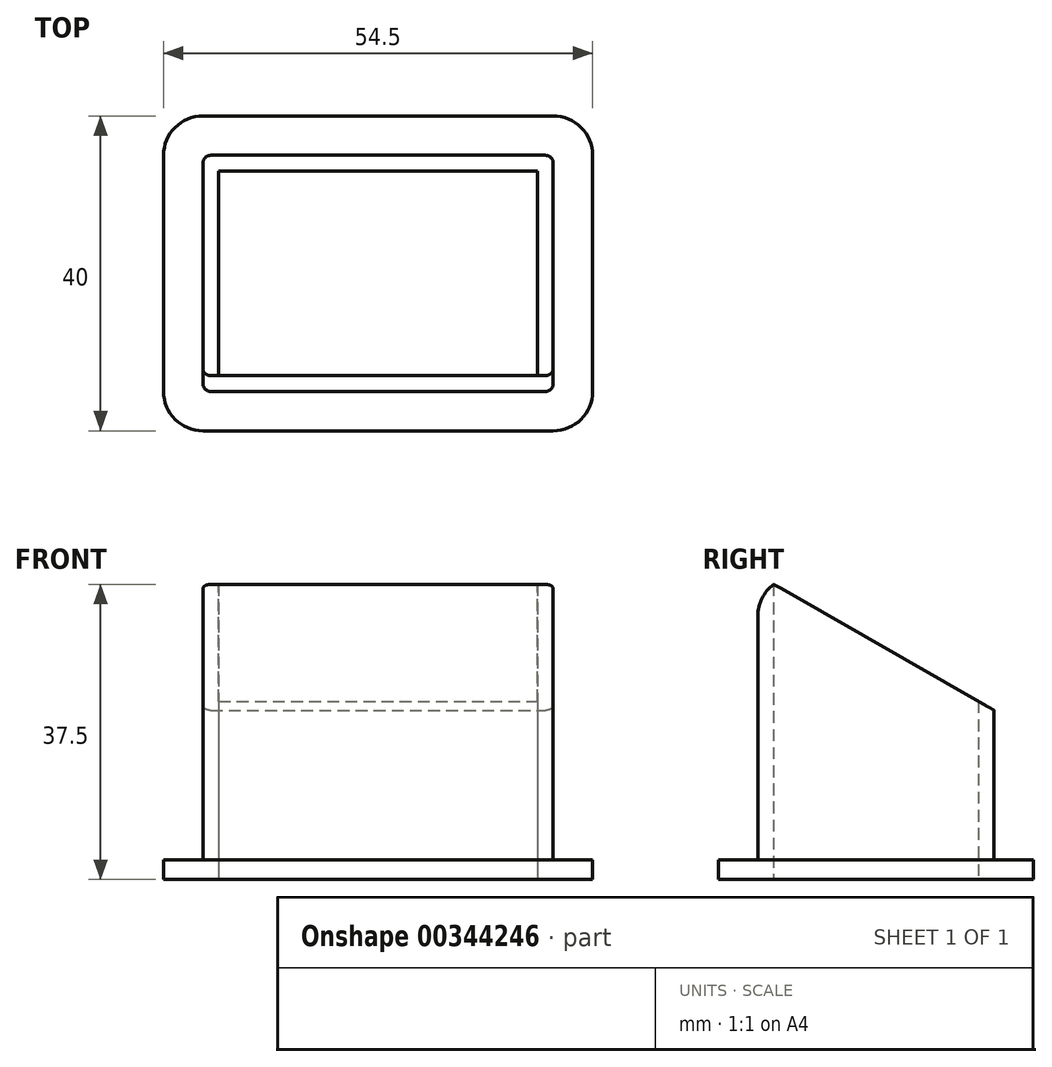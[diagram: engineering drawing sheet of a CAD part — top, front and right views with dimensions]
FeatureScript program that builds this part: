
annotation { "Feature Type Name" : "Feature", "Feature Type Description" : "" }
export const myFeature = defineFeature(function(context is Context, id is Id, definition is map)
    precondition{}
    {
        {
            var Q0;
            Q0=qCreatedBy(makeId("Top.planeOp"),FACE);
            var sketch = newSketch(context, id + "F0", { "sketchPlane" : qUnion([Q0])});
            skLineSegment(sketch, "E0.bottom", {"start": v(-27.25, 20) * mm, "end": v(27.25, 20) * mm});
            skLineSegment(sketch, "E0.top", {"start": v(-27.25, -20) * mm, "end": v(27.25, -20) * mm});
            skLineSegment(sketch, "E0.left", {"start": v(-27.25, 20) * mm, "end": v(-27.25, -20) * mm});
            skLineSegment(sketch, "E0.right", {"start": v(27.25, 20) * mm, "end": v(27.25, -20) * mm});
            skPoint(sketch, "E0.middle", {"position": v(0, 0) * mm});
            skSolve(sketch);
        }
        {
            var Q0;
            Q0=makeQuery(id+"F0.imprint","IMPRINT",FACE,{"disambiguationData":[TD([[makeQuery(id+"F0.imprint","IMPRINT",EDGE,{"derivedFrom":sQuery(id+"F0.wireOp",EDGE,"E0.bottom")}),-1.0]])]});
            extrude(context, id + "F1", {"entities" : qUnion([Q0]), "depth" : 2.5 * mm});
        }
        {
            var Q0;
            Q0=makeQuery(id+"F1.opExtrude","CAP_FACE",FACE,{"disambiguationData":[OSD([sQuery(id+"F0.wireOp",EDGE,"E0.bottom"),sQuery(id+"F0.wireOp",EDGE,"E0.top"),sQuery(id+"F0.wireOp",EDGE,"E0.left"),sQuery(id+"F0.wireOp",EDGE,"E0.right")])],"isStart":false});
            var sketch = newSketch(context, id + "F2", { "sketchPlane" : qUnion([Q0])});
            skLineSegment(sketch, "E1.bottom", {"start": v(-22.25, 15) * mm, "end": v(22.25, 15) * mm});
            skLineSegment(sketch, "E1.top", {"start": v(-22.25, -15) * mm, "end": v(22.25, -15) * mm});
            skLineSegment(sketch, "E1.left", {"start": v(-22.25, 15) * mm, "end": v(-22.25, -15) * mm});
            skLineSegment(sketch, "E1.right", {"start": v(22.25, 15) * mm, "end": v(22.25, -15) * mm});
            skPoint(sketch, "E1.middle", {"position": v(0, 0) * mm});
            skSolve(sketch);
        }
        {
            var Q0;
            Q0 = qSketchRegion(id + "F2", true);
            extrude(context, id + "F3", {"entities" : qUnion([Q0]), "operationType" : NewBodyOperationType.ADD, "depth" : 35 * mm});
        }
        {
            var Q0;
            Q0=makeQuery(id+"F3.opExtrude","CAP_FACE",FACE,{"disambiguationData":[OSD([sQuery(id+"F2.wireOp",EDGE,"E1.bottom"),sQuery(id+"F2.wireOp",EDGE,"E1.top"),sQuery(id+"F2.wireOp",EDGE,"E1.left"),sQuery(id+"F2.wireOp",EDGE,"E1.right")])],"isStart":false});
            shell(context, id + "F4", {"entities" : qUnion([Q0]), "thickness" : 2 * mm});
        }
        {
            var Q0;
            Q0=makeQuery(id+"F4.opShell","OFFSET_FACE",FACE,{"disambiguationData":[OSD([sQuery(id+"F0.wireOp",EDGE,"E0.bottom"),sQuery(id+"F0.wireOp",EDGE,"E0.top"),sQuery(id+"F0.wireOp",EDGE,"E0.left"),sQuery(id+"F0.wireOp",EDGE,"E0.right")])]});
            extrude(context, id + "F5", {"entities" : qUnion([Q0]), "operationType" : NewBodyOperationType.REMOVE, "oppositeDirection" : true, "depth" : 2 * mm});
        }
        {
            var Q0;
            Q0=makeQuery(id+"F3.opExtrude","SWEPT_FACE",FACE,{"disambiguationData":[OSD([sQuery(id+"F2.wireOp",EDGE,"E1.right")])]});
            var sketch = newSketch(context, id + "F6", { "sketchPlane" : qUnion([Q0])});
            skLineSegment(sketch, "E2", {"start": v(15, 2.5) * mm, "end": v(15, 21.5) * mm, "construction": true});
            skLineSegment(sketch, "E3", {"start": v(-15, 37.5) * mm, "end": v(-13, 37.5) * mm, "construction": true});
            skLineSegment(sketch, "E4", {"start": v(15, 21.5) * mm, "end": v(-13, 37.5) * mm});
            skLineSegment(sketch, "E5", {"start": v(-13, 37.5) * mm, "end": v(15, 37.5) * mm});
            skLineSegment(sketch, "E6", {"start": v(15, 37.5) * mm, "end": v(15, 21.5) * mm});
            skSolve(sketch);
        }
        {
            var Q0;
            Q0=makeQuery(id+"F6.imprint","IMPRINT",FACE,{"disambiguationData":[TD([[makeQuery(id+"F6.imprint","IMPRINT",EDGE,{"derivedFrom":sQuery(id+"F6.wireOp",EDGE,"E4")}),-1.0]])]});
            extrude(context, id + "F7", {"entities" : qUnion([Q0]), "operationType" : NewBodyOperationType.REMOVE, "oppositeDirection" : true, "depth" : 45 * mm});
        }
        {
            var Q0;
            Q0=makeQuery(id+"F1.opExtrude","SWEPT_EDGE",EDGE,{"disambiguationData":[OSD([sQuery(id+"F0.wireOp",EDGE,"E0.bottom"),sQuery(id+"F0.wireOp",EDGE,"E0.right")])]});
            var Q1;
            Q1=makeQuery(id+"F1.opExtrude","SWEPT_EDGE",EDGE,{"disambiguationData":[OSD([sQuery(id+"F0.wireOp",EDGE,"E0.top"),sQuery(id+"F0.wireOp",EDGE,"E0.right")])]});
            var Q2;
            Q2=makeQuery(id+"F1.opExtrude","SWEPT_EDGE",EDGE,{"disambiguationData":[OSD([sQuery(id+"F0.wireOp",EDGE,"E0.bottom"),sQuery(id+"F0.wireOp",EDGE,"E0.left")])]});
            var Q3;
            Q3=makeQuery(id+"F1.opExtrude","SWEPT_EDGE",EDGE,{"disambiguationData":[OSD([sQuery(id+"F0.wireOp",EDGE,"E0.top"),sQuery(id+"F0.wireOp",EDGE,"E0.left")])]});
            var Q4;
            Q4=makeQuery(id+"F7.boolean.opBoolean","COPY",EDGE,{"derivedFrom":makeQuery(id+"F7.opExtrude","SWEPT_EDGE",EDGE,{"disambiguationData":[OSD([sQuery(id+"F2.wireOp",EDGE,"E1.bottom"),sQuery(id+"F2.wireOp",EDGE,"E1.right"),sQuery(id+"F6.wireOp",EDGE,"E4"),sQuery(id+"F6.wireOp",EDGE,"E6")])]})});
            var Q5;
            Q5=makeQuery(id+"F3.opExtrude","CAP_EDGE",EDGE,{"disambiguationData":[OSD([sQuery(id+"F2.wireOp",EDGE,"E1.top")])],"isStart":false});
            fillet(context, id + "F8", {"entities" : qUnion([Q0, Q1, Q2, Q3, Q4, Q5]), "radius" : 5 * mm, "tangentPropagation" : true, "allowEdgeOverflow" : false});
        }
        {
            var Q0;
            Q0=makeQuery(id+"F3.opExtrude","SWEPT_EDGE",EDGE,{"disambiguationData":[OSD([sQuery(id+"F2.wireOp",EDGE,"E1.bottom"),sQuery(id+"F2.wireOp",EDGE,"E1.right")])]});
            var Q1;
            Q1=makeQuery(id+"F3.opExtrude","SWEPT_EDGE",EDGE,{"disambiguationData":[OSD([sQuery(id+"F2.wireOp",EDGE,"E1.top"),sQuery(id+"F2.wireOp",EDGE,"E1.right")])]});
            var Q2;
            Q2=makeQuery(id+"F8.opFillet","BLEND_EDGE",EDGE,{"blendedFrom":[makeQuery(id+"F3.opExtrude","CAP_EDGE",EDGE,{"disambiguationData":[OSD([sQuery(id+"F2.wireOp",EDGE,"E1.top")])],"isStart":false}),makeQuery(id+"F3.opExtrude","SWEPT_FACE",FACE,{"disambiguationData":[OSD([sQuery(id+"F2.wireOp",EDGE,"E1.left")])]})],"blendedInto":[makeQuery(id+"F3.opExtrude","SWEPT_FACE",FACE,{"disambiguationData":[OSD([sQuery(id+"F2.wireOp",EDGE,"E1.left")])]})]});
            var Q3;
            Q3=makeQuery(id+"F3.opExtrude","SWEPT_EDGE",EDGE,{"disambiguationData":[OSD([sQuery(id+"F2.wireOp",EDGE,"E1.bottom"),sQuery(id+"F2.wireOp",EDGE,"E1.left")])]});
            var Q4;
            Q4=makeQuery(id+"F5.boolean.opBoolean","COPY",EDGE,{"derivedFrom":makeQuery(id+"F5.opExtrude","CAP_EDGE",EDGE,{"disambiguationData":[OSD([sQuery(id+"F0.wireOp",EDGE,"E0.bottom"),sQuery(id+"F0.wireOp",EDGE,"E0.top"),sQuery(id+"F0.wireOp",EDGE,"E0.left"),sQuery(id+"F0.wireOp",EDGE,"E0.right"),sQuery(id+"F2.wireOp",EDGE,"E1.top")])],"isStart":false})});
            var Q5;
            Q5=makeQuery(id+"F5.boolean.opBoolean","COPY",EDGE,{"derivedFrom":makeQuery(id+"F5.opExtrude","CAP_EDGE",EDGE,{"disambiguationData":[OSD([sQuery(id+"F0.wireOp",EDGE,"E0.bottom"),sQuery(id+"F0.wireOp",EDGE,"E0.top"),sQuery(id+"F0.wireOp",EDGE,"E0.left"),sQuery(id+"F0.wireOp",EDGE,"E0.right"),sQuery(id+"F2.wireOp",EDGE,"E1.left")])],"isStart":false})});
            var Q6;
            Q6=makeQuery(id+"F5.boolean.opBoolean","COPY",EDGE,{"derivedFrom":makeQuery(id+"F5.opExtrude","CAP_EDGE",EDGE,{"disambiguationData":[OSD([sQuery(id+"F0.wireOp",EDGE,"E0.bottom"),sQuery(id+"F0.wireOp",EDGE,"E0.top"),sQuery(id+"F0.wireOp",EDGE,"E0.left"),sQuery(id+"F0.wireOp",EDGE,"E0.right"),sQuery(id+"F2.wireOp",EDGE,"E1.bottom")])],"isStart":false})});
            var Q7;
            Q7=makeQuery(id+"F5.boolean.opBoolean","COPY",EDGE,{"derivedFrom":makeQuery(id+"F5.opExtrude","CAP_EDGE",EDGE,{"disambiguationData":[OSD([sQuery(id+"F0.wireOp",EDGE,"E0.bottom"),sQuery(id+"F0.wireOp",EDGE,"E0.top"),sQuery(id+"F0.wireOp",EDGE,"E0.left"),sQuery(id+"F0.wireOp",EDGE,"E0.right"),sQuery(id+"F2.wireOp",EDGE,"E1.right")])],"isStart":false})});
            var Q8;
            {var subQ0=sQuery(id+"F2.wireOp",EDGE,"E1.bottom");Q8=makeQuery(id+"F8.opFillet","BLEND_EDGE",EDGE,{"blendedFrom":[makeQuery(id+"F7.boolean.opBoolean","COPY",EDGE,{"derivedFrom":makeQuery(id+"F7.opExtrude","SWEPT_EDGE",EDGE,{"disambiguationData":[OSD([subQ0,sQuery(id+"F2.wireOp",EDGE,"E1.right"),sQuery(id+"F6.wireOp",EDGE,"E4"),sQuery(id+"F6.wireOp",EDGE,"E6")])]})}),makeQuery(id+"F5.boolean.opBoolean","MERGE",FACE,{"derivedFrom":[makeQuery(id+"F4.opShell","OFFSET_FACE",FACE,{"disambiguationData":[OSD([subQ0])]}),makeQuery(id+"F5.opExtrude","SWEPT_FACE",FACE,{"disambiguationData":[OSD([sQuery(id+"F0.wireOp",EDGE,"E0.bottom"),sQuery(id+"F0.wireOp",EDGE,"E0.top"),sQuery(id+"F0.wireOp",EDGE,"E0.left"),sQuery(id+"F0.wireOp",EDGE,"E0.right"),subQ0])]})]})],"blendedInto":[makeQuery(id+"F5.boolean.opBoolean","MERGE",FACE,{"derivedFrom":[makeQuery(id+"F4.opShell","OFFSET_FACE",FACE,{"disambiguationData":[OSD([subQ0])]}),makeQuery(id+"F5.opExtrude","SWEPT_FACE",FACE,{"disambiguationData":[OSD([sQuery(id+"F0.wireOp",EDGE,"E0.bottom"),sQuery(id+"F0.wireOp",EDGE,"E0.top"),sQuery(id+"F0.wireOp",EDGE,"E0.left"),sQuery(id+"F0.wireOp",EDGE,"E0.right"),subQ0])]})]})]});}
            fillet(context, id + "F9", {"entities" : qUnion([Q0, Q1, Q2, Q3, Q4, Q5, Q6, Q7, Q8]), "radius" : 1 * mm, "tangentPropagation" : true, "allowEdgeOverflow" : false});
        }
    });
